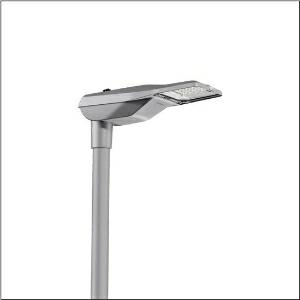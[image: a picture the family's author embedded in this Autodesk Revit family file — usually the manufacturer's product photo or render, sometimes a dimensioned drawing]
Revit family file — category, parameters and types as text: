
# Revit family: streetlight_sl_21_micro___pl52_5xe1h43s08db_6aa2
name_source: partatom
category: Lighting Fixtures
units: mm (PartAtom-declared; Revit-internal decimal feet)

## family parameters
Cut with Voids When Loaded = No
Host = Face
Light Source = No
Part Type = Normal
Room Calculation Point = No
Round Connector Dimension = Use Diameter
Shared = No

## types (1)
- --- (1 x LED, 5230 lm, 39.1 W, 4000K)
    Apparent Load = 39 VA
    CIE Flux Codes = 27 59 98 100 100
    Color Rendering = 70
    Color Temperature = 4000K
    Default Elevation = 1800 mm
    Description = Streetlight SL 21 micro, mast luminaire, primary light control with lens, of PMMA, primary optical cover: cover, of toughened safety glass, transparent, light distribution: PL52, light emission: direct distribution, primary light characteristic: asymmetric, installation type: side-entry, post-top, LED, High Power LED, rated luminous flux: 5.230lm, luminous efficacy: 134lm/W, light colour: 740, colour temperature: 4000K, control gear: D4i, control: flexible luminous flux parameterisation, time-dependent luminous flux control, constant luminous flux control, overheat protection, pre-setting: logarithmic dimming characteristic, mains connection: 220..240V, AC, 50/60Hz, start of lifetime: 39W, end of service life: 41W, reduction: 18W, luminaire housing, of diecast aluminium, powder-coated, SITECO metallic grey (DB 702S), corrosivity category C5 high according to DIN EN ISO 12944, please order mast flange separately, inclination adjustable: 0°, 5°, 10°, 15°, sealing non-destructively replaceable, multi-level sealing system, length: 528mm, width: 235mm, height: 110mm, mast flange for spigot size: 42mm (side-entry): 5XC10008XM4, 60/48mm (side-entry/post-top): 5XC10108XM2, 76/60mm (side-entry/post-top): 5XC10108XM1, Smart Interface above, protection rating (complete): IP66, insulation class (complete): insulation class II (safety insulation), certification: CE, ENEC, ENEC+, VDE, impact resistance: IK10, permissible operating ambient temperature for outdoor applications: -40..+50°C, standard-compliant lighting for roads and squares, packaging unit: 1 piece

Light Distribution: PL52
    Height = 110 mm
    Lamp = 1 x LED
    Lamp Light Flux = 5230 lm
    Lamp Power = 39.1 W
    Lamp count = 1
    Length = 528 mm
    Luminous efficacy = 134 lm/W
    Manufacturer = Siteco
    ModVariant = No
    Model = 5XE1H43S08DB
    Number of Poles = 1
    OnlyDefault = Yes
    Power Factor = 1
    Product Name = Streetlight SL 21 micro | PL52
    Product group = mast luminaire | pylon top
    ProductGroupID = 6100
    Protection Class = Protection class II
    Protection Degree = IP 66
    RLX_Detail_Level = 1
    RLX_Emergency_Light_Flux = 0 lm
    RLX_Emergency_Type = 0
    RLX_Emergency_Type_DB = No
    RlxData = <blob elided: 108281 chars, md5=82835439>
    Socket = socket
    Standby Power = 0 W
    System Light Flux = 5230 lm
    System Power = 39 W
    Type Comments = factory setting: luminous flux: 100 % | dim-lin: 254 | 765 mA
    Type Image = l_1277292.jpg
    URL = http://relux.com
    VarID = @adj_155703
    Voltage = 0 V
    Weight = 0.00 kg
    Width = 235 mm

## geometry (parser evidence)
native form markers: Blend x4, Sweep x8
no freeform markers — native parametric forms only
